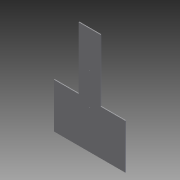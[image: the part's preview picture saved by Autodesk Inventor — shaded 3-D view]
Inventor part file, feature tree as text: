
AUTODESK INVENTOR PART (.ipt)
format: ipt  version: 2011 (Build 150239000, 239)  size: 172,544 bytes
history: native  units: in
note: dims shown in document units (in); Inventor stores cm internally (conversion verified against a paired STEP export)
features: extrude x13, sketch x13
ambient origin geometry x8: Origin, YZ Plane, XZ Plane, XY Plane, X Axis, Y Axis, Z Axis, Center Point
bodies: Solid1 (feature_tree)
feature tree (26):
  extrude  "Extrusion1"  Depth=35.0in
  extrude  "Extrusion2"  Depth=7.0in
  extrude  "Extrusion3"  Depth=7.0in
  extrude  "Extrusion4"  Depth=1.0in TaperAngle=0.0deg
  extrude  "Extrusion5"  Depth=0.25in TaperAngle=0.0deg
  extrude  "Extrusion6"  Depth=19.638in
  extrude  "Extrusion7"  Depth=1.0in TaperAngle=0.0deg
  extrude  "Extrusion8"  Depth=0.185in
  extrude  "Extrusion9"  Depth=15.0in
  extrude  "Extrusion10"  Depth=1.0in TaperAngle=0.0deg
  extrude  "Extrusion11"  Depth=12.5in
  extrude  "Extrusion12"  Depth=0.25in TaperAngle=0.0deg
  extrude  "Extrusion13"  Depth=3.86in
  sketch  "Sketch1"  dims[d0=20.248in d1=35.0in]
  sketch  "Sketch3"  dims[d2=0.25in d3=0.0in d4=7.0in]
  sketch  "Sketch4"  dims[d5=18.14in d6=7.0in]
  sketch  "Sketch5"  dims[d7=18.14in d8=1.0in d9=0.0in]
  sketch  "Sketch6"  dims[d10=0.25in d11=0.0in d12=0.25in d13=0.0in]
  sketch  "Sketch7"  dims[d14=0.25in d15=0.0in d16=19.638in]
  sketch  "Sketch8"  dims[d17=0.185in d18=1.0in d19=0.0in]
  sketch  "Sketch9"  dims[d20=9.075in d21=0.185in]
  sketch  "Sketch10"  dims[d22=1.0in d23=0.0in d24=15.0in]
  sketch  "Sketch11"  dims[d25=0.612in d26=1.0in d27=0.0in]
  sketch  "Sketch12"  dims[d28=0.25in d29=0.0in d30=12.5in]
  sketch  "Sketch13"  dims[d31=0.25in d32=0.25in d33=0.0in]
  sketch  "Sketch14"  dims[d34=3.86in d35=3.86in d36=0.25in d37=0.0in d38=0.25in d39=0.0in d40=0.75in d41=1.0in d42=0.0in]
